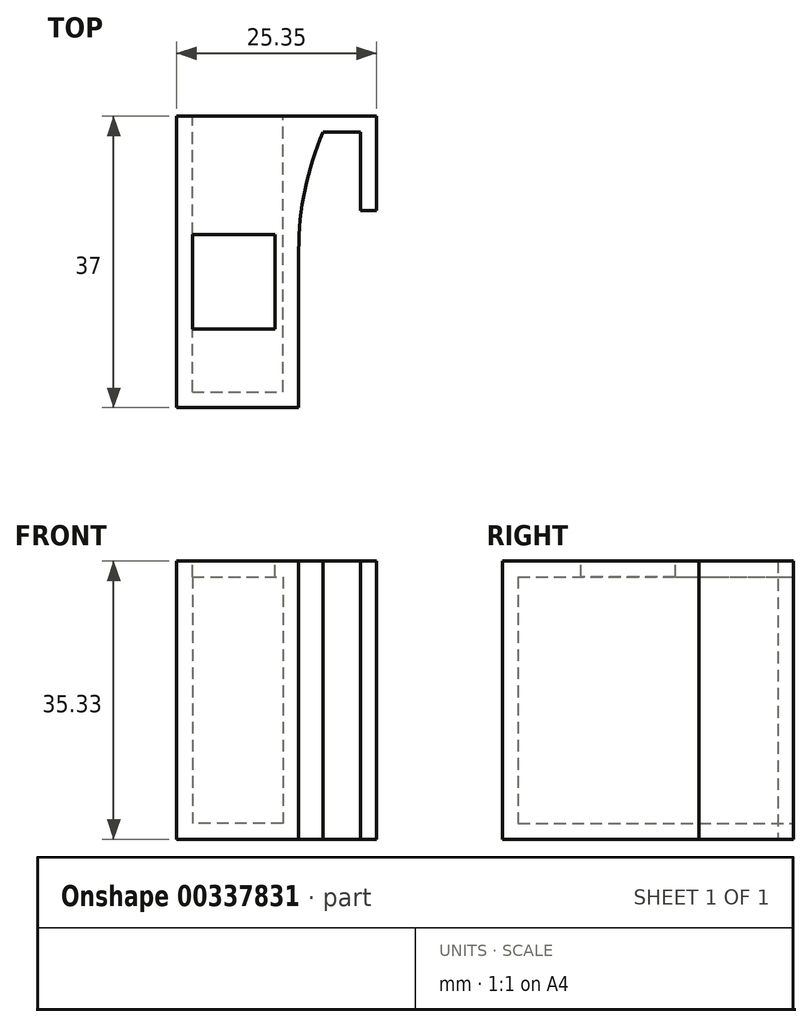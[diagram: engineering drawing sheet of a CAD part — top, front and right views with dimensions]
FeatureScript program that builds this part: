
annotation { "Feature Type Name" : "Feature", "Feature Type Description" : "" }
export const myFeature = defineFeature(function(context is Context, id is Id, definition is map)
    precondition{}
    {
        {
            var Q0;
            Q0=qCreatedBy(makeId("Top.planeOp"),FACE);
            var sketch = newSketch(context, id + "F0", { "sketchPlane" : qUnion([Q0])});
            skLineSegment(sketch, "E0", {"start": v(0, 0) * mm, "end": v(0, 37) * mm});
            skLineSegment(sketch, "E1", {"start": v(0, 37) * mm, "end": v(25.35, 37) * mm});
            skLineSegment(sketch, "E2", {"start": v(25.35, 37) * mm, "end": v(25.35, 25) * mm});
            skLineSegment(sketch, "E3", {"start": v(25.35, 25) * mm, "end": v(23.35, 25) * mm});
            skLineSegment(sketch, "E4", {"start": v(23.35, 25) * mm, "end": v(23.35, 35) * mm});
            skLineSegment(sketch, "E5", {"start": v(15.5, 0) * mm, "end": v(0, 0) * mm});
            skLineSegment(sketch, "E6", {"start": v(23.35, 35) * mm, "end": v(18.6, 35) * mm});
            skArc(sketch, "E7", {"start": v(18.6, 35) * mm, "mid": v(16.28, 27.66) * mm, "end": v(15.5, 20) * mm});
            skLineSegment(sketch, "E8", {"start": v(15.5, 20) * mm, "end": v(15.5, 0) * mm});
            skSolve(sketch);
        }
        {
            var Q0;
            Q0=makeQuery(id+"F0.imprint","IMPRINT",FACE,{"disambiguationData":[TD([[makeQuery(id+"F0.imprint","IMPRINT",EDGE,{"derivedFrom":sQuery(id+"F0.wireOp",EDGE,"E0")}),-1.0]])]});
            extrude(context, id + "F1", {"entities" : qUnion([Q0]), "depth" : 35.33 * mm});
        }
        {
            var Q0;
            Q0=makeQuery(id+"F1.opExtrude","SWEPT_FACE",FACE,{"disambiguationData":[OSD([sQuery(id+"F0.wireOp",EDGE,"E1")])]});
            var sketch = newSketch(context, id + "F2", { "sketchPlane" : qUnion([Q0])});
            skLineSegment(sketch, "E9.1", {"start": v(-2, 33.33) * mm, "end": v(-2, 2) * mm});
            skLineSegment(sketch, "E10", {"start": v(-2, 33.33) * mm, "end": v(-13.5, 33.33) * mm});
            skLineSegment(sketch, "E11", {"start": v(-13.5, 33.33) * mm, "end": v(-13.5, 2) * mm});
            skLineSegment(sketch, "E12", {"start": v(-13.5, 2) * mm, "end": v(-2, 2) * mm});
            skSolve(sketch);
        }
        {
            var Q0;
            Q0=makeQuery(id+"F2.imprint","IMPRINT",FACE,{"disambiguationData":[TD([[makeQuery(id+"F2.imprint","IMPRINT",EDGE,{"derivedFrom":sQuery(id+"F2.wireOp",EDGE,"E9.1")}),-1.0]])]});
            extrude(context, id + "F3", {"entities" : qUnion([Q0]), "operationType" : NewBodyOperationType.REMOVE, "oppositeDirection" : true, "depth" : 35 * mm});
        }
        {
            var Q0;
            Q0=makeQuery(id+"F1.opExtrude","CAP_FACE",FACE,{"disambiguationData":[OSD([sQuery(id+"F0.wireOp",EDGE,"E0"),sQuery(id+"F0.wireOp",EDGE,"E1"),sQuery(id+"F0.wireOp",EDGE,"E2"),sQuery(id+"F0.wireOp",EDGE,"E3"),sQuery(id+"F0.wireOp",EDGE,"E4"),sQuery(id+"F0.wireOp",EDGE,"E5"),sQuery(id+"F0.wireOp",EDGE,"E6"),sQuery(id+"F0.wireOp",EDGE,"E7"),sQuery(id+"F0.wireOp",EDGE,"E8")])],"isStart":false});
            var sketch = newSketch(context, id + "F4", { "sketchPlane" : qUnion([Q0])});
            skLineSegment(sketch, "E13", {"start": v(2, 10) * mm, "end": v(2, 22) * mm});
            skLineSegment(sketch, "E14", {"start": v(2, 22) * mm, "end": v(12.5, 22) * mm});
            skLineSegment(sketch, "E15", {"start": v(12.5, 22) * mm, "end": v(12.5, 10) * mm});
            skLineSegment(sketch, "E16", {"start": v(12.5, 10) * mm, "end": v(2, 10) * mm});
            skSolve(sketch);
        }
        {
            var Q0;
            Q0=makeQuery(id+"F4.imprint","IMPRINT",FACE,{"disambiguationData":[TD([[makeQuery(id+"F4.imprint","IMPRINT",EDGE,{"derivedFrom":sQuery(id+"F4.wireOp",EDGE,"E13")}),-1.0]])]});
            extrude(context, id + "F5", {"entities" : qUnion([Q0]), "operationType" : NewBodyOperationType.REMOVE, "oppositeDirection" : true, "depth" : 2 * mm});
        }
    });
